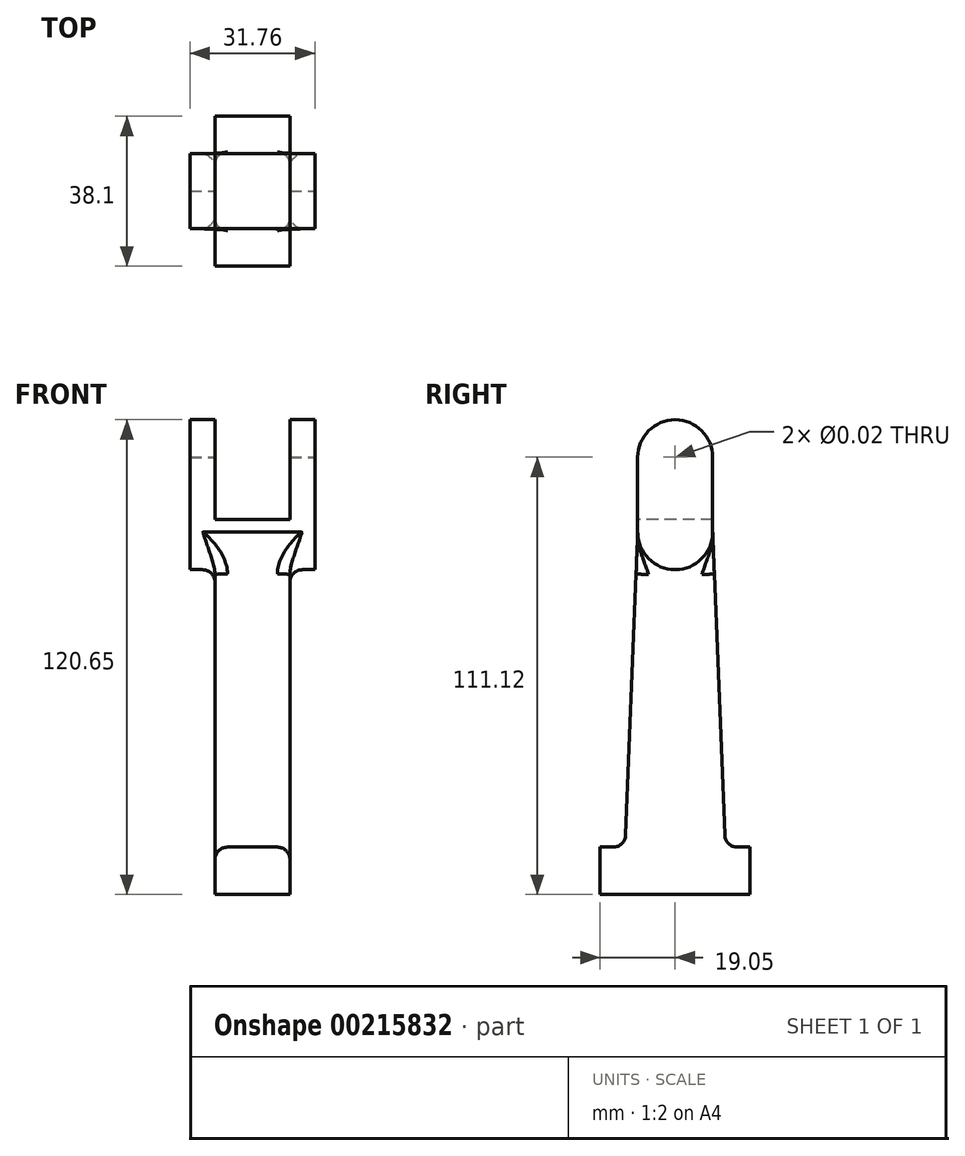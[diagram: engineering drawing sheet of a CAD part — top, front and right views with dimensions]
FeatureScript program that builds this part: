
annotation { "Feature Type Name" : "Feature", "Feature Type Description" : "" }
export const myFeature = defineFeature(function(context is Context, id is Id, definition is map)
    precondition{}
    {
        {
            var Q0;
            Q0=qCreatedBy(makeId("Right.planeOp"),FACE);
            var sketch = newSketch(context, id + "F0", { "sketchPlane" : qUnion([Q0])});
            skLineSegment(sketch, "E0", {"start": v(-9.53, 0) * mm, "end": v(-9.52, -19.05) * mm});
            skLineSegment(sketch, "E1", {"start": v(-9.52, -19.05) * mm, "end": v(-12.58, -96) * mm});
            skLineSegment(sketch, "E2", {"start": v(-15.75, -99.05) * mm, "end": v(-19.05, -99.05) * mm});
            skLineSegment(sketch, "E3", {"start": v(-19.05, -99.05) * mm, "end": v(-19.05, -111.13) * mm});
            skLineSegment(sketch, "E4", {"start": v(-19.05, -111.13) * mm, "end": v(0, -111.13) * mm});
            skLineSegment(sketch, "E5", {"start": v(0, -111.13) * mm, "end": v(0, 7.33) * mm});
            skLineSegment(sketch, "E6", {"start": v(0, 7.33) * mm, "end": v(0, 9.53) * mm});
            skArc(sketch, "E7", {"start": v(-9.53, 0) * mm, "mid": v(-6.74, 6.74) * mm, "end": v(0, 9.53) * mm});
            skPoint(sketch, "E8.visualSharp", {"position": v(-12.7, -99.05) * mm});
            skArc(sketch, "E8.filletArc", {"start": v(-15.75, -99.05) * mm, "mid": v(-13.55, -98.16) * mm, "end": v(-12.58, -96) * mm});
            skArc(sketch, "E9.MirrorCS", {"start": v(9.53, 0) * mm, "mid": v(6.74, 6.74) * mm, "end": v(0, 9.53) * mm});
            skLineSegment(sketch, "E10.MirrorCS", {"start": v(9.53, 0) * mm, "end": v(9.52, -19.05) * mm});
            skLineSegment(sketch, "E11.MirrorCS", {"start": v(9.52, -19.05) * mm, "end": v(12.58, -96) * mm});
            skLineSegment(sketch, "E12.MirrorCS", {"start": v(15.75, -99.05) * mm, "end": v(19.05, -99.05) * mm});
            skArc(sketch, "E13.MirrorCS", {"start": v(15.75, -99.05) * mm, "mid": v(13.55, -98.16) * mm, "end": v(12.58, -96) * mm});
            skLineSegment(sketch, "E14.MirrorCS", {"start": v(19.05, -99.05) * mm, "end": v(19.05, -111.13) * mm});
            skLineSegment(sketch, "E15.MirrorCS", {"start": v(19.05, -111.13) * mm, "end": v(0, -111.13) * mm});
            skPoint(sketch, "E16", {"position": v(0, -19.05) * mm});
            skArc(sketch, "E17", {"start": v(-9.52, -19.05) * mm, "mid": v(0, -28.57) * mm, "end": v(9.52, -19.05) * mm});
            skSolve(sketch);
        }
        {
            var Q0;
            Q0=qSketchRegion(id+"F0",true);
            var Q1;
            Q1=qConstructionFilter(qBodyType(qCreatedBy(id+"F0",EDGE),BodyType.WIRE),ConstructionObject.NO);
            extrude(context, id + "F1", {"entities" : qUnion([Q0]), "surfaceEntities" : qUnion([Q1]), "endBound" : BoundingType.SYMMETRIC, "depth" : 19.05 * mm});
        }
        {
            var Q0;
            {var subQ1=sQuery(id+"F0.wireOp",EDGE,"E6");Q0=makeQuery(id+"F0.imprint","IMPRINT",FACE,{"disambiguationData":[TD([[makeQuery(id+"F0.imprint","IMPRINT",EDGE,{"derivedFrom":subQ1}),-1.0]])]});}
            var Q1;
            {var subQ4=sQuery(id+"F0.wireOp",EDGE,"E0");Q1=makeQuery(id+"F0.imprint","IMPRINT",FACE,{"disambiguationData":[TD([[makeQuery(id+"F0.imprint","IMPRINT",EDGE,{"derivedFrom":subQ4}),1.0]])]});}
            extrude(context, id + "F2", {"entities" : qUnion([Q0, Q1]), "operationType" : NewBodyOperationType.ADD, "endBound" : BoundingType.SYMMETRIC, "depth" : 31.75 * mm});
        }
        {
            var Q0;
            Q0=makeQuery(id+"F2.boolean.opBoolean","INTERSECT",EDGE,{"derivedFrom":[makeQuery(id+"F1.opExtrude","CAP_FACE",FACE,{"disambiguationData":[OSD([sQuery(id+"F0.wireOp",EDGE,"E0"),sQuery(id+"F0.wireOp",EDGE,"E1"),sQuery(id+"F0.wireOp",EDGE,"E2"),sQuery(id+"F0.wireOp",EDGE,"E3"),sQuery(id+"F0.wireOp",EDGE,"E4"),sQuery(id+"F0.wireOp",EDGE,"E7"),sQuery(id+"F0.wireOp",EDGE,"E8.filletArc"),sQuery(id+"F0.wireOp",EDGE,"E9.MirrorCS"),sQuery(id+"F0.wireOp",EDGE,"E10.MirrorCS"),sQuery(id+"F0.wireOp",EDGE,"E11.MirrorCS"),sQuery(id+"F0.wireOp",EDGE,"E12.MirrorCS"),sQuery(id+"F0.wireOp",EDGE,"E13.MirrorCS"),sQuery(id+"F0.wireOp",EDGE,"E14.MirrorCS"),sQuery(id+"F0.wireOp",EDGE,"E15.MirrorCS")])],"isStart":false}),makeQuery(id+"F2.opExtrude","SWEPT_FACE",FACE,{"disambiguationData":[OSD([sQuery(id+"F0.wireOp",EDGE,"E17")])]})]});
            var Q1;
            Q1=makeQuery(id+"F2.boolean.opBoolean","INTERSECT",EDGE,{"derivedFrom":[makeQuery(id+"F1.opExtrude","CAP_FACE",FACE,{"disambiguationData":[OSD([sQuery(id+"F0.wireOp",EDGE,"E0"),sQuery(id+"F0.wireOp",EDGE,"E1"),sQuery(id+"F0.wireOp",EDGE,"E2"),sQuery(id+"F0.wireOp",EDGE,"E3"),sQuery(id+"F0.wireOp",EDGE,"E4"),sQuery(id+"F0.wireOp",EDGE,"E7"),sQuery(id+"F0.wireOp",EDGE,"E8.filletArc"),sQuery(id+"F0.wireOp",EDGE,"E9.MirrorCS"),sQuery(id+"F0.wireOp",EDGE,"E10.MirrorCS"),sQuery(id+"F0.wireOp",EDGE,"E11.MirrorCS"),sQuery(id+"F0.wireOp",EDGE,"E12.MirrorCS"),sQuery(id+"F0.wireOp",EDGE,"E13.MirrorCS"),sQuery(id+"F0.wireOp",EDGE,"E14.MirrorCS"),sQuery(id+"F0.wireOp",EDGE,"E15.MirrorCS")])],"isStart":true}),makeQuery(id+"F2.opExtrude","SWEPT_FACE",FACE,{"disambiguationData":[OSD([sQuery(id+"F0.wireOp",EDGE,"E17")])]})]});
            fillet(context, id + "F3", {"entities" : qUnion([Q0, Q1]), "radius" : 3.17 * mm, "tangentPropagation" : true, "allowEdgeOverflow" : false});
        }
        {
            var Q0;
            Q0=makeQuery(id+"F1.opExtrude","CAP_EDGE",EDGE,{"disambiguationData":[OSD([sQuery(id+"F0.wireOp",EDGE,"E11.MirrorCS")])],"isStart":false});
            var Q1;
            Q1=makeQuery(id+"F1.opExtrude","CAP_EDGE",EDGE,{"disambiguationData":[OSD([sQuery(id+"F0.wireOp",EDGE,"E11.MirrorCS")])],"isStart":true});
            var Q2;
            Q2=makeQuery(id+"F1.opExtrude","CAP_EDGE",EDGE,{"disambiguationData":[OSD([sQuery(id+"F0.wireOp",EDGE,"E1")])],"isStart":true});
            var Q3;
            Q3=makeQuery(id+"F1.opExtrude","CAP_EDGE",EDGE,{"disambiguationData":[OSD([sQuery(id+"F0.wireOp",EDGE,"E1")])],"isStart":false});
            fillet(context, id + "F4", {"entities" : qUnion([Q0, Q1, Q2, Q3]), "radius" : 3.17 * mm, "tangentPropagation" : true, "allowEdgeOverflow" : false});
        }
        {
            var Q0;
            Q0=makeQuery(id+"F2.opExtrude","CAP_FACE",FACE,{"disambiguationData":[OSD([sQuery(id+"F0.wireOp",EDGE,"E0"),sQuery(id+"F0.wireOp",EDGE,"E7"),sQuery(id+"F0.wireOp",EDGE,"E9.MirrorCS"),sQuery(id+"F0.wireOp",EDGE,"E10.MirrorCS"),sQuery(id+"F0.wireOp",EDGE,"E17")])],"isStart":false});
            var sketch = newSketch(context, id + "F5", { "sketchPlane" : qUnion([Q0])});
            skPoint(sketch, "E18.0", {"position": v(0, 0) * mm});
            skSolve(sketch);
        }
        {
            var Q0;
            Q0=sQuery(id+"F5.wireOp",VERTEX,"E18.0");
            var Q1;
            Q1=makeQuery(id+"F1.opExtrude","SWEPT_BODY",BODY,{"disambiguationData":[OSD([sQuery(id+"F0.wireOp",EDGE,"E0"),sQuery(id+"F0.wireOp",EDGE,"E1"),sQuery(id+"F0.wireOp",EDGE,"E2"),sQuery(id+"F0.wireOp",EDGE,"E3"),sQuery(id+"F0.wireOp",EDGE,"E4"),sQuery(id+"F0.wireOp",EDGE,"E7"),sQuery(id+"F0.wireOp",EDGE,"E8.filletArc"),sQuery(id+"F0.wireOp",EDGE,"E9.MirrorCS"),sQuery(id+"F0.wireOp",EDGE,"E10.MirrorCS"),sQuery(id+"F0.wireOp",EDGE,"E11.MirrorCS"),sQuery(id+"F0.wireOp",EDGE,"E12.MirrorCS"),sQuery(id+"F0.wireOp",EDGE,"E13.MirrorCS"),sQuery(id+"F0.wireOp",EDGE,"E14.MirrorCS"),sQuery(id+"F0.wireOp",EDGE,"E15.MirrorCS")])]});
            hole(context, id + "F6", {"style" : HoleStyle.SIMPLE, "endStyle" : HoleEndStyle.BLIND, "standardTappedOrClearance" : lookupTablePath({ "standard" : "ANSI", "size" : "1/2 (0.5)", "type" : "Drilled" }), "standardBlindInLast" : lookupTablePath({ "standard" : "ANSI", "size" : "1/2", "type" : "Drilled" }), "holeDiameter" : 1 / 50.8 * mm, "holeDepth" : 34.3 * mm, "startFromSketch" : true, "locations" : qUnion([Q0]), "scope" : qUnion([Q1])});
        }
        {
            var Q0;
            Q0=qCreatedBy(makeId("Right.planeOp"),FACE);
            var sketch = newSketch(context, id + "F7", { "sketchPlane" : qUnion([Q0])});
            skArc(sketch, "E19.0", {"start": v(9.53, 0) * mm, "mid": v(6.74, 6.74) * mm, "end": v(0, 9.53) * mm});
            skArc(sketch, "E20.0", {"start": v(-9.53, 0) * mm, "mid": v(-6.74, 6.74) * mm, "end": v(0, 9.53) * mm});
            skLineSegment(sketch, "E21.0", {"start": v(-9.53, 0) * mm, "end": v(-9.52, -19.05) * mm});
            skPoint(sketch, "E22.0", {"position": v(9.52, -9.53) * mm});
            skLineSegment(sketch, "E23.0", {"start": v(9.53, 0) * mm, "end": v(9.52, -19.05) * mm});
            skLineSegment(sketch, "E24", {"start": v(9.52, -15.88) * mm, "end": v(-9.52, -15.88) * mm});
            skSolve(sketch);
        }
        {
            var Q0;
            Q0=qSketchRegion(id+"F7",true);
            extrude(context, id + "F8", {"entities" : qUnion([Q0]), "operationType" : NewBodyOperationType.REMOVE, "endBound" : BoundingType.SYMMETRIC, "oppositeDirection" : true, "depth" : 19.05 * mm});
        }
    });
